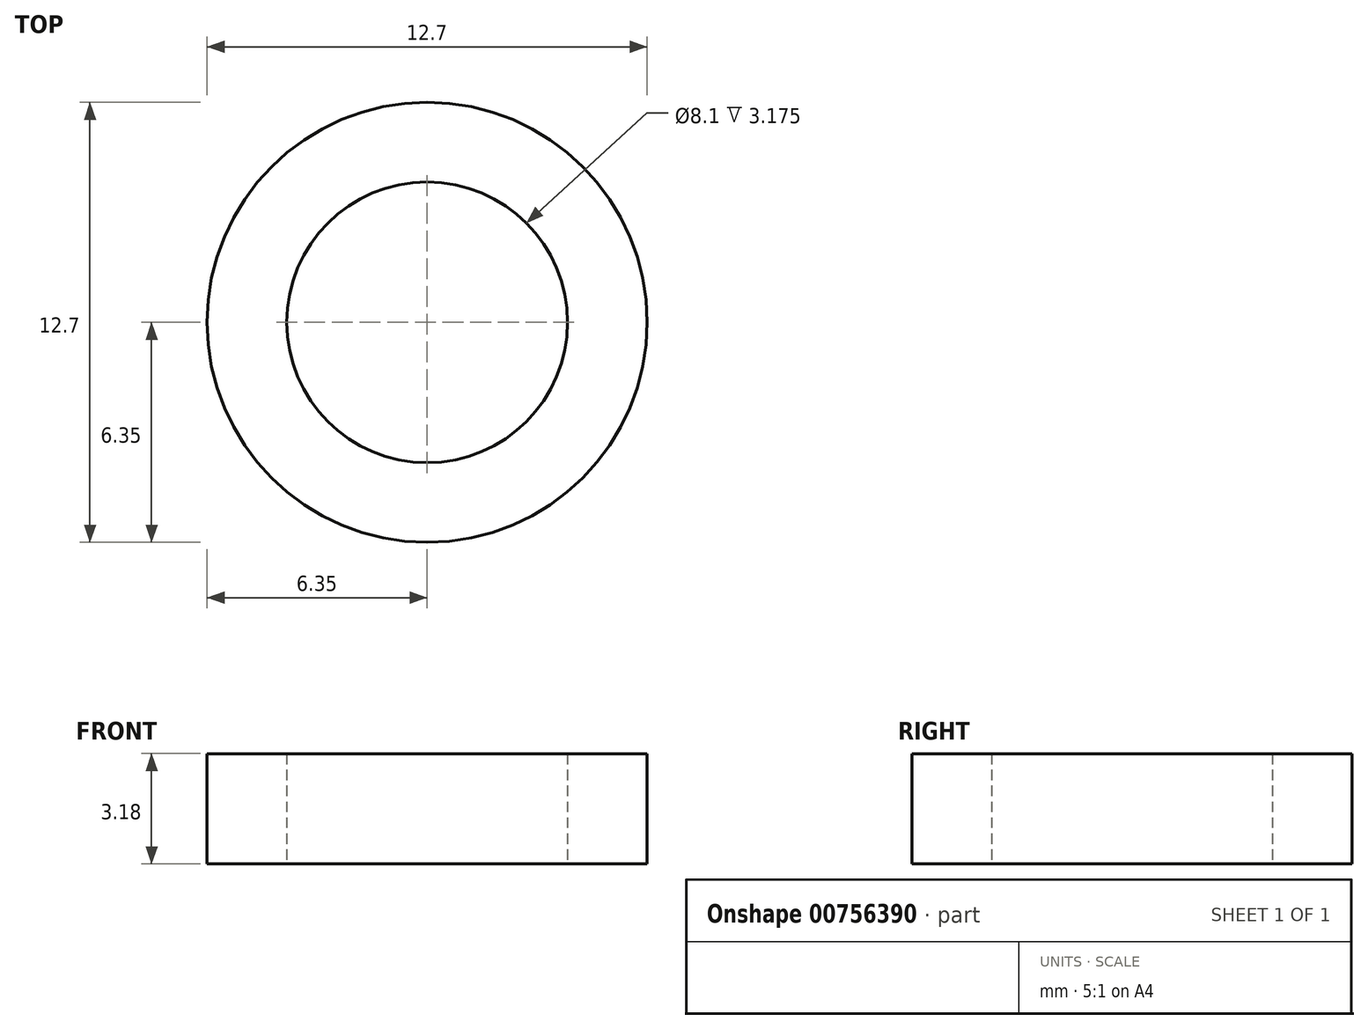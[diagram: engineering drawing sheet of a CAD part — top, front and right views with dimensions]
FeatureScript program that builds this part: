
annotation { "Feature Type Name" : "Feature", "Feature Type Description" : "" }
export const myFeature = defineFeature(function(context is Context, id is Id, definition is map)
    precondition{}
    {
        {
            var Q0;
            Q0=qCreatedBy(makeId("Top.planeOp"),FACE);
            var sketch = newSketch(context, id + "F0", { "sketchPlane" : qUnion([Q0])});
            skCircle(sketch, "E0", {"center": v(0, 0) * mm, "radius": 6.35 * mm});
            skCircle(sketch, "E1", {"center": v(0, 0) * mm, "radius": 4.05 * mm});
            skSolve(sketch);
        }
        {
            var Q0;
            Q0=makeQuery(id+"F0.imprint","IMPRINT",FACE,{"disambiguationData":[TD([[makeQuery(id+"F0.imprint","IMPRINT",EDGE,{"derivedFrom":sQuery(id+"F0.wireOp",EDGE,"E0")}),1.0]])]});
            extrude(context, id + "F1", {"entities" : qUnion([Q0]), "depth" : 3.17 * mm, "offsetDistance" : 25.4 * mm});
        }
    });
